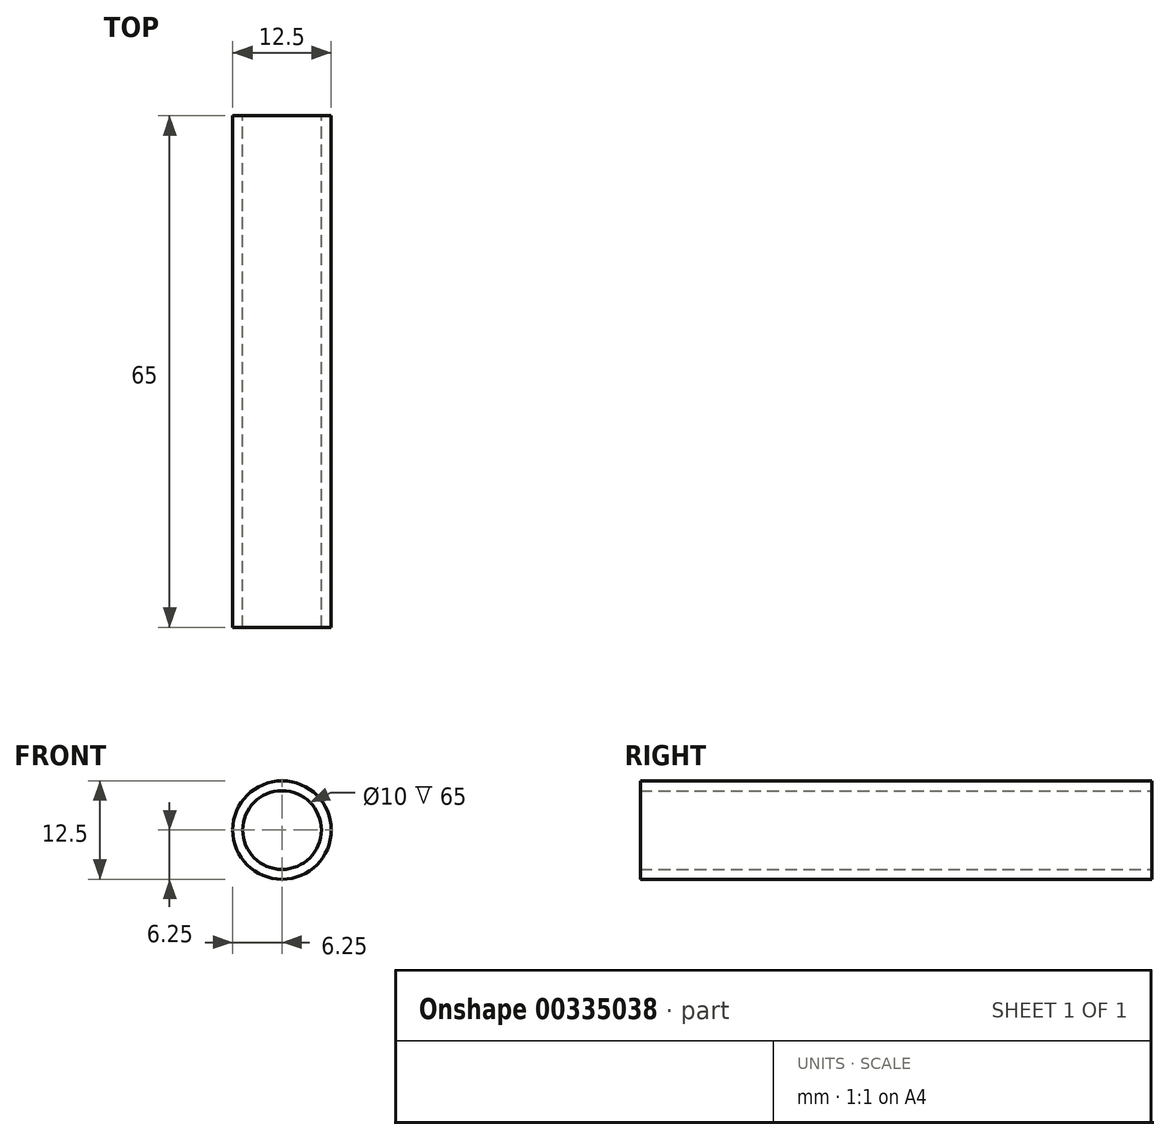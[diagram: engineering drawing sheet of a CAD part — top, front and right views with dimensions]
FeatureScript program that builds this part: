
annotation { "Feature Type Name" : "Feature", "Feature Type Description" : "" }
export const myFeature = defineFeature(function(context is Context, id is Id, definition is map)
    precondition{}
    {
        {
            var Q0;
            Q0=qCreatedBy(makeId("Front.planeOp"),FACE);
            var sketch = newSketch(context, id + "F0", { "sketchPlane" : qUnion([Q0])});
            skCircle(sketch, "E0", {"center": v(0, 0) * mm, "radius": 5 * mm});
            skCircle(sketch, "E1", {"center": v(0, 0) * mm, "radius": 6.25 * mm});
            skSolve(sketch);
        }
        {
            var Q0;
            Q0=makeQuery(id+"F0.imprint","IMPRINT",FACE,{"disambiguationData":[TD([[makeQuery(id+"F0.imprint","IMPRINT",EDGE,{"derivedFrom":sQuery(id+"F0.wireOp",EDGE,"E0")}),-1.0]])]});
            extrude(context, id + "F1", {"entities" : qUnion([Q0]), "depth" : 65 * mm});
        }
    });
